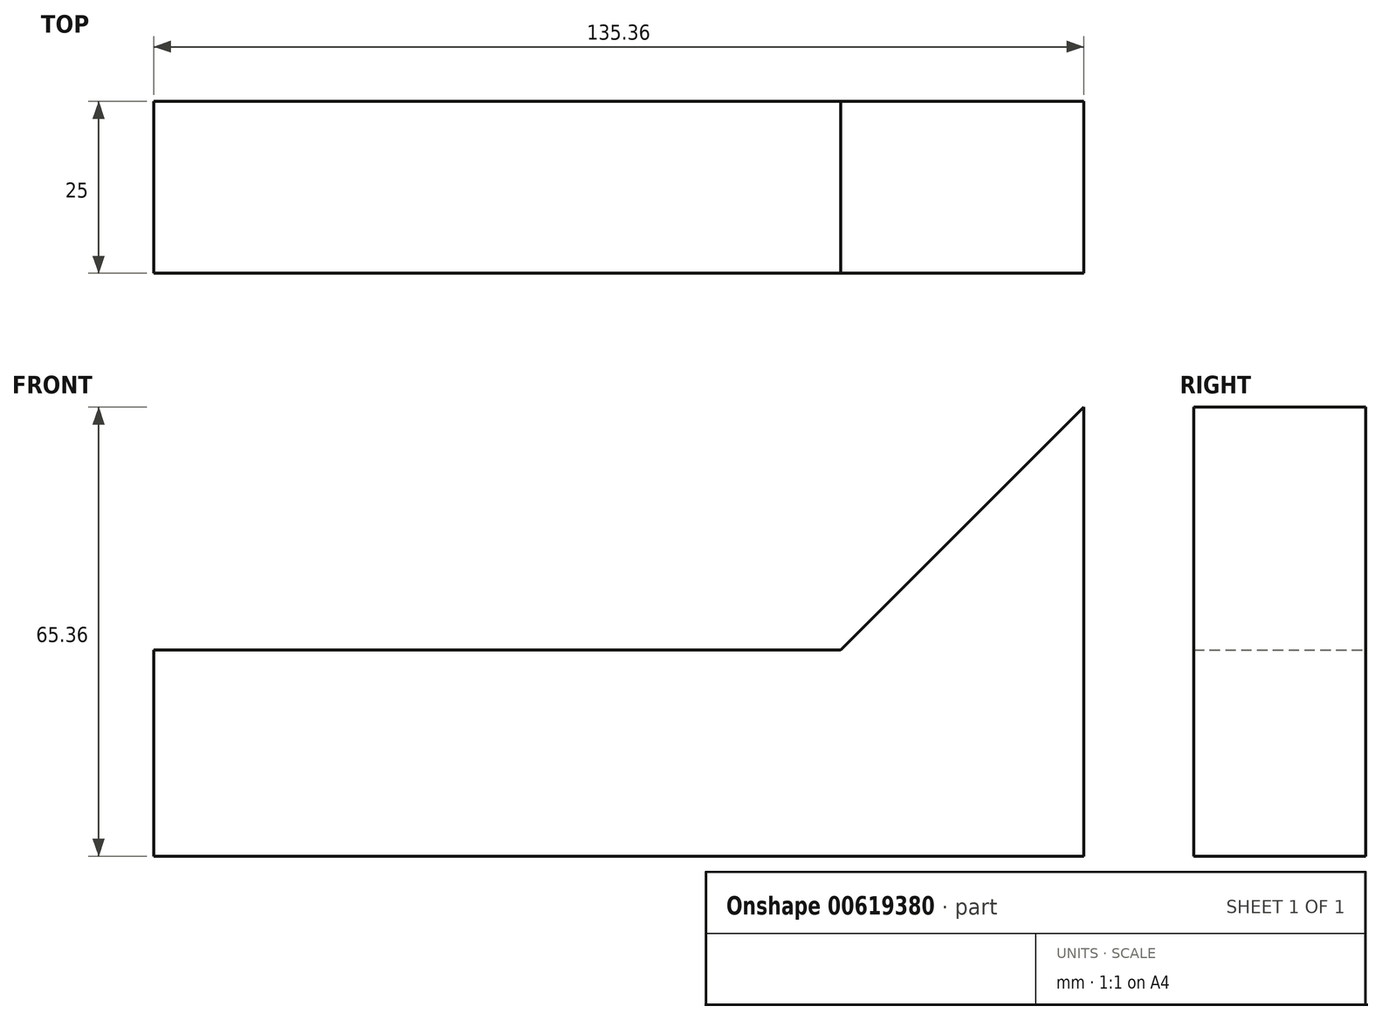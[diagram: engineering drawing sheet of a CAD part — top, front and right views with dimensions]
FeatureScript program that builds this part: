
annotation { "Feature Type Name" : "Feature", "Feature Type Description" : "" }
export const myFeature = defineFeature(function(context is Context, id is Id, definition is map)
    precondition{}
    {
        {
            var Q0;
            Q0=qCreatedBy(makeId("Front.planeOp"),FACE);
            var sketch = newSketch(context, id + "F0", { "sketchPlane" : qUnion([Q0])});
            skLineSegment(sketch, "E0.top", {"start": v(-5.36, 30) * mm, "end": v(-105.36, 30) * mm});
            skLineSegment(sketch, "E0.right", {"start": v(-105.36, 0) * mm, "end": v(-105.36, 30) * mm});
            skLineSegment(sketch, "E1", {"start": v(-5.36, 30) * mm, "end": v(30, 65.36) * mm});
            skLineSegment(sketch, "E2", {"start": v(30, 65.36) * mm, "end": v(30, 0) * mm});
            skLineSegment(sketch, "E3", {"start": v(30, 0) * mm, "end": v(0, 0) * mm});
            skLineSegment(sketch, "E4", {"start": v(-105.36, 0) * mm, "end": v(0, 0) * mm});
            skSolve(sketch);
        }
        {
            var Q0;
            Q0 = qSketchRegion(id + "F0", true);
            extrude(context, id + "F1", {"entities" : qUnion([Q0]), "depth" : 25 * mm, "offsetDistance" : 25 * mm});
        }
    });
